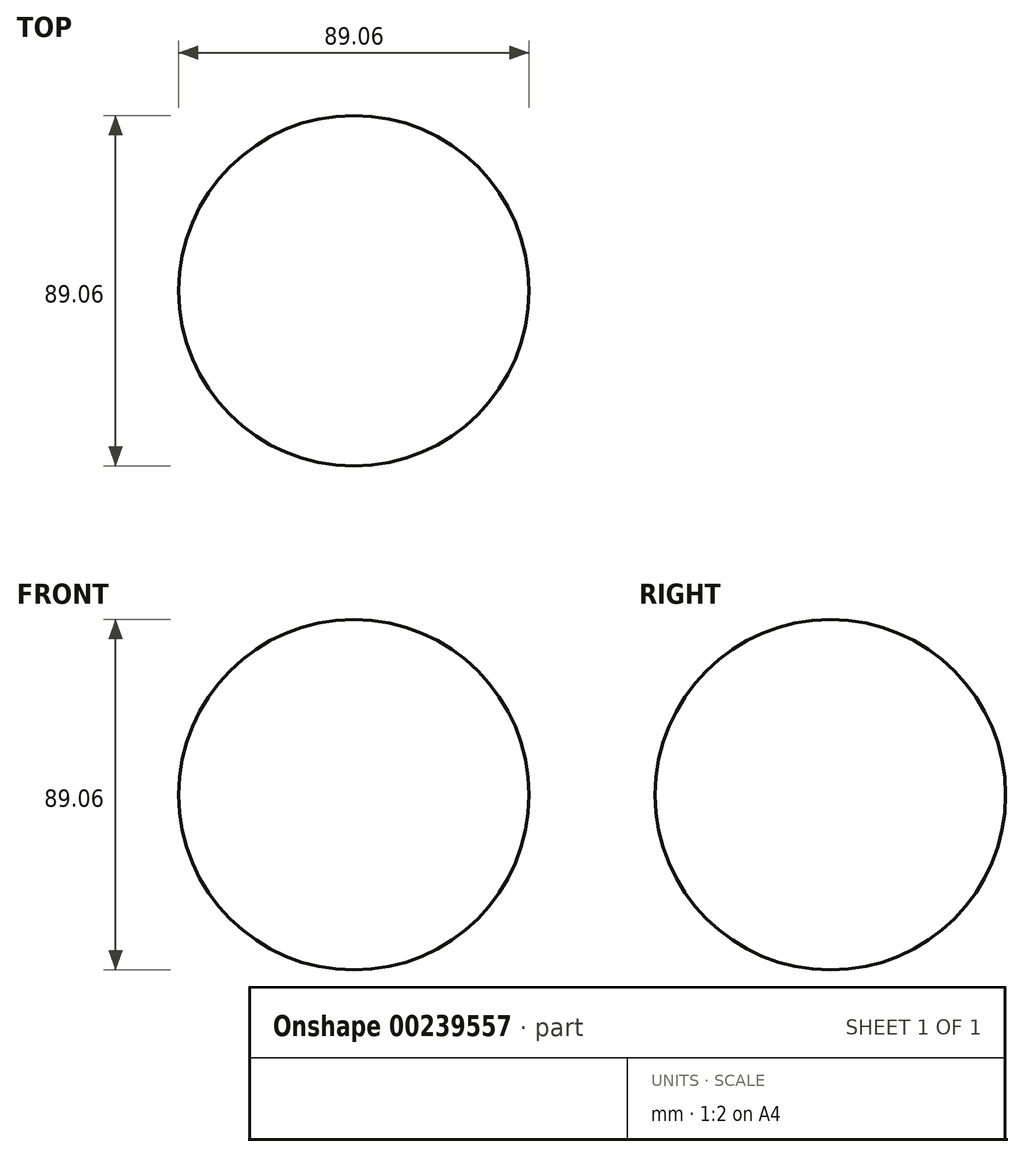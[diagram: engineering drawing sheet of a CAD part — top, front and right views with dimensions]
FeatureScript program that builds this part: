
annotation { "Feature Type Name" : "Feature", "Feature Type Description" : "" }
export const myFeature = defineFeature(function(context is Context, id is Id, definition is map)
    precondition{}
    {
        {
            var Q0;
            Q0=qCreatedBy(makeId("Front.planeOp"),FACE);
            var sketch = newSketch(context, id + "F0", { "sketchPlane" : qUnion([Q0])});
            skArc(sketch, "E0", {"start": v(0, -44.53) * mm, "mid": v(44.53, 0) * mm, "end": v(0, 44.53) * mm});
            skLineSegment(sketch, "E1", {"start": v(0, 44.53) * mm, "end": v(0, -44.53) * mm});
            skSolve(sketch);
        }
        {
            var Q0;
            Q0 = qSketchRegion(id + "F0", true);
            var Q1;
            Q1=sQuery(id+"F0.wireOp",EDGE,"E1");
            revolve(context, id + "F1", {"entities" : qUnion([Q0]), "axis" : qUnion([Q1]), "revolveType" : RevolveType.FULL});
        }
    });
